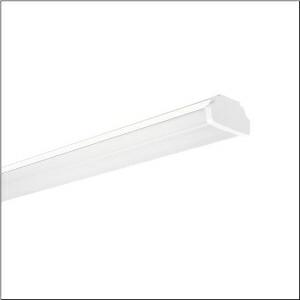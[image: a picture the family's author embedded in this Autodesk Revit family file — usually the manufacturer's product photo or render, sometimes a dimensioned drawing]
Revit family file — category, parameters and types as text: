
# Revit family: modario_r__31_ho_53bm812c1v4105_deab
name_source: partatom
category: Lighting Fixtures
units: mm (PartAtom-declared; Revit-internal decimal feet)

## family parameters
Cut with Voids When Loaded = No
Host = Face
Light Source = No
Part Type = Normal
Room Calculation Point = No
Round Connector Dimension = Use Diameter
Shared = No

## types (1)
- --- (1 x LED, 10520 lm, 63.8 W, 4000K)
    Apparent Load = 64 VA
    CIE Flux Codes = 47 80 95 92 100
    Color Rendering = 80
    Color Temperature = 4000K
    Default Elevation = 1800 mm
    Description = Modario® 31 HOluminaire insert, length: 1.495mm, width: 81mm, height: 82mm, LED rated luminous flux: 10.520lm, light colour: 840, control gear: ON/OFF Multilumen, CLOi, control gear: ECG Multilumen, with plug, 3-pole, with phase selection, mains connection: 220..240V, AC, 50/60Hz, primary optical cover: cover, of PMMA, light emission: direct distribution, primary light characteristic: symmetric, protection rating (complete): IP20, protection rating (LED compartment): IP50, insulation class (complete): insulation class I (protective earthing), certification: CE, ENEC, VDE, UKCA, permissible ambient temperature for indoor applications: -35..+35°C, corresponds to IFS (International Featured Standards) requirements for safety and quality in the food industry, reducing of maximum allowable ambient temperature of 5°C with ceiling mounting, packaging unit: 1 piece
    Height = 92 mm
    Lamp = 1 x LED
    Lamp Light Flux = 10520 lm
    Lamp Power = 63.8 W
    Lamp count = 1
    Length = 1495 mm
    Luminous efficacy = 165 lm/W
    Manufacturer = Siteco
    ModVariant = No
    Model = 53BM812C1V4105
    Mounting Place = Ceiling
    Mounting Type = Pendant
    Number of Poles = 1
    OnlyDefault = Yes
    Power Factor = 1
    Product Name = Modario® 31 HO
    Product group = luminaire insert
    ProductGroupID = 902
    Protection Class = Protection class I
    Protection Degree = IP 20
    RLX_Detail_Level = 1
    RlxData = <blob elided: 39789 chars, md5=bd73afe6>
    Socket = socket
    Standby Power = 0 W
    System Light Flux = 10520 lm
    System Power = 64 W
    Type Comments = factory setting: luminous flux: 100 % | (A | C | E) | 144 mA
    Type Image = l_1003447.jpg
    URL = http://relux.com
    VarID = @adj_131301
    Voltage = 0 V
    Weight = 0.00 kg
    Width = 81 mm

## geometry (parser evidence)
native form markers: Blend x4, Sweep x12
no freeform markers — native parametric forms only
